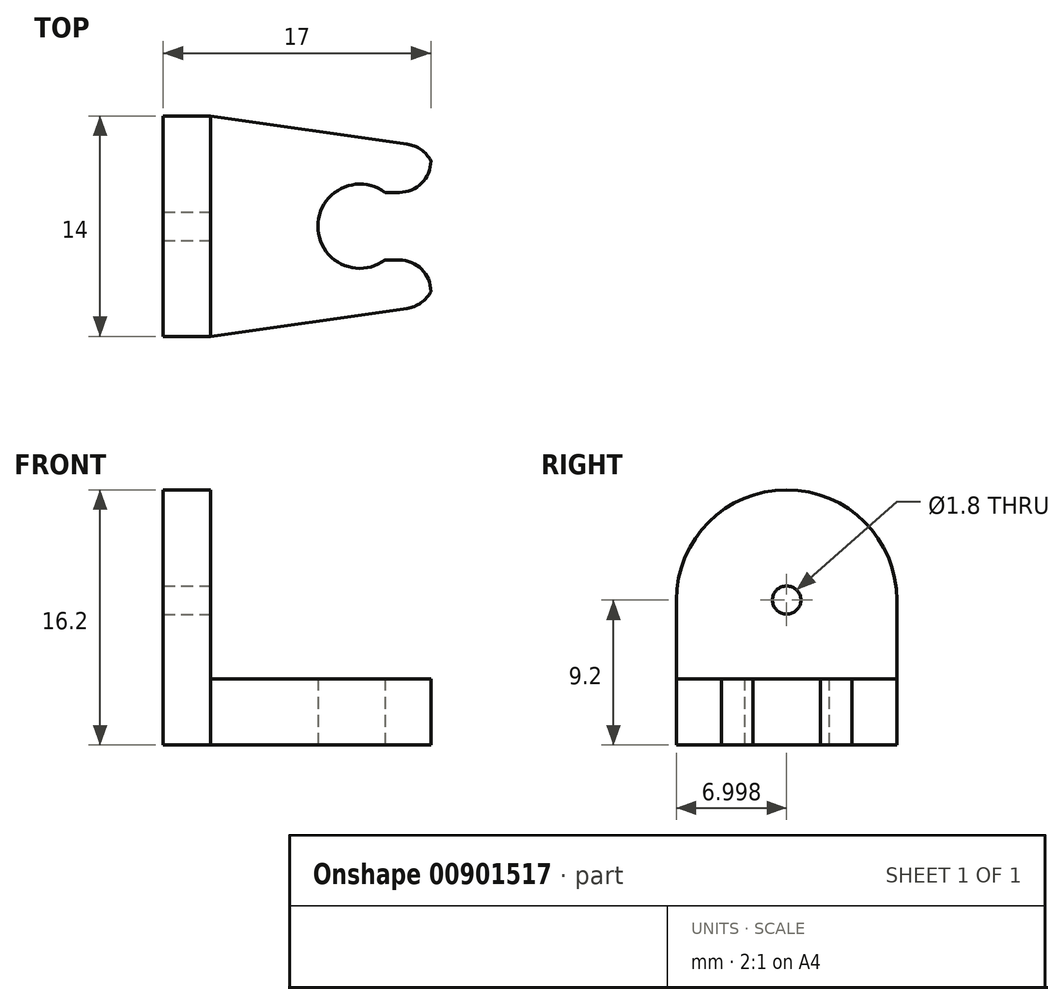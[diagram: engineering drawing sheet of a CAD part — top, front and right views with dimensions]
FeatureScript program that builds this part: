
annotation { "Feature Type Name" : "Feature", "Feature Type Description" : "" }
export const myFeature = defineFeature(function(context is Context, id is Id, definition is map)
    precondition{}
    {
        {
            var Q0;
            Q0=qCreatedBy(makeId("Top.planeOp"),FACE);
            var sketch = newSketch(context, id + "F0", { "sketchPlane" : qUnion([Q0])});
            skLineSegment(sketch, "E0.bottom", {"start": v(-13.65, 5.37) * mm, "end": v(3.35, 5.37) * mm});
            skLineSegment(sketch, "E0.top", {"start": v(-13.65, -8.63) * mm, "end": v(3.35, -8.63) * mm});
            skLineSegment(sketch, "E0.left", {"start": v(-13.65, 5.37) * mm, "end": v(-13.65, -8.63) * mm});
            skLineSegment(sketch, "E0.right", {"start": v(3.35, 5.37) * mm, "end": v(3.35, -8.63) * mm});
            skPoint(sketch, "E1", {"position": v(-1.15, -1.63) * mm});
            skCircle(sketch, "E2", {"center": v(-1.15, -1.63) * mm, "radius": 2.67 * mm});
            skLineSegment(sketch, "E3", {"start": v(3.35, -3.78) * mm, "end": v(0.44, -3.78) * mm});
            skLineSegment(sketch, "E4", {"start": v(0.44, 0.52) * mm, "end": v(3.35, 0.52) * mm});
            skSolve(sketch);
        }
        {
            var Q0;
            {var subQ1=sQuery(id+"F0.wireOp",EDGE,"E0.bottom");Q0=makeQuery(id+"F0.imprint","IMPRINT",FACE,{"disambiguationData":[TD([[makeQuery(id+"F0.imprint","IMPRINT",EDGE,{"derivedFrom":subQ1}),-1.0]])]});}
            extrude(context, id + "F1", {"entities" : qUnion([Q0]), "depth" : 4.2 * mm, "offsetDistance" : 25 * mm});
        }
        {
            var Q0;
            Q0=makeQuery(id+"F1.opExtrude","SWEPT_EDGE",EDGE,{"disambiguationData":[OSD([sQuery(id+"F0.wireOp",EDGE,"E0.bottom"),sQuery(id+"F0.wireOp",EDGE,"E0.right")])]});
            chamfer(context, id + "F2", {"entities" : qUnion([Q0]), "chamferType" : ChamferType.TWO_OFFSETS, "width1" : 14 * mm, "oppositeDirection" : false, "width2" : 2 * mm, "tangentPropagation" : true});
        }
        {
            var Q0;
            Q0=makeQuery(id+"F1.opExtrude","SWEPT_EDGE",EDGE,{"disambiguationData":[OSD([sQuery(id+"F0.wireOp",EDGE,"E0.top"),sQuery(id+"F0.wireOp",EDGE,"E0.right")])]});
            chamfer(context, id + "F3", {"entities" : qUnion([Q0]), "chamferType" : ChamferType.TWO_OFFSETS, "width1" : 2 * mm, "oppositeDirection" : false, "width2" : 14 * mm, "tangentPropagation" : true});
        }
        {
            var Q0;
            Q0=makeQuery(id+"F1.opExtrude","SWEPT_EDGE",EDGE,{"disambiguationData":[OSD([sQuery(id+"F0.wireOp",EDGE,"E0.right"),sQuery(id+"F0.wireOp",EDGE,"E4")])]});
            fillet(context, id + "F4", {"entities" : qUnion([Q0]), "radius" : 2 * mm, "tangentPropagation" : true, "allowEdgeOverflow" : false});
        }
        {
            var Q0;
            {var subQ0=sQuery(id+"F0.wireOp",EDGE,"E0.right");var subQ1=sQuery(id+"F0.wireOp",EDGE,"E0.bottom");Q0=makeQuery(id+"F2.opChamfer","BLEND_EDGE",EDGE,{"blendedFrom":[makeQuery(id+"F1.opExtrude","SWEPT_EDGE",EDGE,{"disambiguationData":[OSD([subQ1,subQ0])]}),makeQuery(id+"F1.opExtrude","SWEPT_FACE",FACE,{"disambiguationData":[OSD([subQ0]),TDD([makeQuery(id+"F0.imprint","IMPRINT",EDGE,{"disambiguationData":[TD([[makeQuery(id+"F0.imprint","INTERSECT",VERTEX,{"derivedFrom":[subQ1,subQ0]}),-1.0]])],"derivedFrom":subQ0})])]})],"blendedInto":[makeQuery(id+"F1.opExtrude","SWEPT_FACE",FACE,{"disambiguationData":[OSD([subQ0]),TDD([makeQuery(id+"F0.imprint","IMPRINT",EDGE,{"disambiguationData":[TD([[makeQuery(id+"F0.imprint","INTERSECT",VERTEX,{"derivedFrom":[subQ1,subQ0]}),-1.0]])],"derivedFrom":subQ0})])]})]});}
            fillet(context, id + "F5", {"entities" : qUnion([Q0]), "radius" : 2 * mm, "tangentPropagation" : true, "allowEdgeOverflow" : false});
        }
        {
            var Q0;
            Q0=makeQuery(id+"F1.opExtrude","SWEPT_EDGE",EDGE,{"disambiguationData":[OSD([sQuery(id+"F0.wireOp",EDGE,"E0.right"),sQuery(id+"F0.wireOp",EDGE,"E3")])]});
            fillet(context, id + "F6", {"entities" : qUnion([Q0]), "radius" : 2 * mm, "tangentPropagation" : true, "allowEdgeOverflow" : false});
        }
        {
            var Q0;
            {var subQ0=sQuery(id+"F0.wireOp",EDGE,"E0.right");var subQ1=sQuery(id+"F0.wireOp",EDGE,"E0.top");Q0=makeQuery(id+"F3.opChamfer","BLEND_EDGE",EDGE,{"blendedFrom":[makeQuery(id+"F1.opExtrude","SWEPT_EDGE",EDGE,{"disambiguationData":[OSD([subQ1,subQ0])]}),makeQuery(id+"F1.opExtrude","SWEPT_FACE",FACE,{"disambiguationData":[OSD([subQ0]),TDD([makeQuery(id+"F0.imprint","IMPRINT",EDGE,{"disambiguationData":[TD([[makeQuery(id+"F0.imprint","INTERSECT",VERTEX,{"derivedFrom":[subQ1,subQ0]}),1.0]])],"derivedFrom":subQ0})])]})],"blendedInto":[makeQuery(id+"F1.opExtrude","SWEPT_FACE",FACE,{"disambiguationData":[OSD([subQ0]),TDD([makeQuery(id+"F0.imprint","IMPRINT",EDGE,{"disambiguationData":[TD([[makeQuery(id+"F0.imprint","INTERSECT",VERTEX,{"derivedFrom":[subQ1,subQ0]}),1.0]])],"derivedFrom":subQ0})])]})]});}
            fillet(context, id + "F7", {"entities" : qUnion([Q0]), "radius" : 2 * mm, "tangentPropagation" : true, "allowEdgeOverflow" : false});
        }
        {
            var Q0;
            Q0=makeQuery(id+"F1.opExtrude","CAP_FACE",FACE,{"disambiguationData":[OSD([sQuery(id+"F0.wireOp",EDGE,"E0.bottom"),sQuery(id+"F0.wireOp",EDGE,"E0.top"),sQuery(id+"F0.wireOp",EDGE,"E0.left"),sQuery(id+"F0.wireOp",EDGE,"E0.right"),sQuery(id+"F0.wireOp",EDGE,"E2"),sQuery(id+"F0.wireOp",EDGE,"E3"),sQuery(id+"F0.wireOp",EDGE,"E4")])],"isStart":false});
            var sketch = newSketch(context, id + "F8", { "sketchPlane" : qUnion([Q0])});
            skLineSegment(sketch, "E5.bottom", {"start": v(-13.65, -8.63) * mm, "end": v(-10.65, -8.63) * mm});
            skLineSegment(sketch, "E5.top", {"start": v(-13.65, 5.37) * mm, "end": v(-10.65, 5.37) * mm});
            skLineSegment(sketch, "E5.left", {"start": v(-13.65, -8.63) * mm, "end": v(-13.65, 5.37) * mm});
            skLineSegment(sketch, "E5.right", {"start": v(-10.65, -8.63) * mm, "end": v(-10.65, 5.37) * mm});
            skSolve(sketch);
        }
        {
            var Q0;
            Q0=makeQuery(id+"F8.imprint","IMPRINT",FACE,{"disambiguationData":[TD([[makeQuery(id+"F8.imprint","IMPRINT",EDGE,{"derivedFrom":sQuery(id+"F8.wireOp",EDGE,"E5.bottom")}),1.0]])]});
            extrude(context, id + "F9", {"entities" : qUnion([Q0]), "operationType" : NewBodyOperationType.ADD, "depth" : 12 * mm, "offsetDistance" : 25 * mm});
        }
        {
            var Q0;
            Q0=makeQuery(id+"F9.opExtrude","CAP_EDGE",EDGE,{"disambiguationData":[OSD([sQuery(id+"F8.wireOp",EDGE,"E5.bottom")])],"isStart":false});
            var Q1;
            Q1=makeQuery(id+"F9.opExtrude","CAP_EDGE",EDGE,{"disambiguationData":[OSD([sQuery(id+"F8.wireOp",EDGE,"E5.top")])],"isStart":false});
            fillet(context, id + "F10", {"entities" : qUnion([Q0, Q1]), "radius" : 7 * mm, "tangentPropagation" : true, "allowEdgeOverflow" : false});
        }
        {
            var Q0;
            Q0=makeQuery(id+"F9.opExtrude","SWEPT_FACE",FACE,{"disambiguationData":[OSD([sQuery(id+"F8.wireOp",EDGE,"E5.right")])]});
            var sketch = newSketch(context, id + "F11", { "sketchPlane" : qUnion([Q0])});
            skPoint(sketch, "E6", {"position": v(-1.63, 9.2) * mm});
            skSolve(sketch);
        }
        {
            var Q0;
            Q0=sQuery(id+"F11.wireOp",VERTEX,"E6");
            var Q1;
            Q1=makeQuery(id+"F1.opExtrude","SWEPT_BODY",BODY,{"disambiguationData":[OSD([sQuery(id+"F0.wireOp",EDGE,"E0.bottom"),sQuery(id+"F0.wireOp",EDGE,"E0.top"),sQuery(id+"F0.wireOp",EDGE,"E0.left"),sQuery(id+"F0.wireOp",EDGE,"E0.right"),sQuery(id+"F0.wireOp",EDGE,"E2"),sQuery(id+"F0.wireOp",EDGE,"E3"),sQuery(id+"F0.wireOp",EDGE,"E4")])]});
            hole(context, id + "F12", {"style" : HoleStyle.SIMPLE, "endStyle" : HoleEndStyle.THROUGH, "holeDiameter" : 1.8 * mm, "majorDiameter" : 5 * mm, "isTappedThrough" : true, "tappedDepth" : 12 * mm, "tapClearance" : 3, "locations" : qUnion([Q0]), "scope" : qUnion([Q1])});
        }
    });
